# Revit family: HUNTER_PROS-04 Stream, Strip and Bubbler Nozzles
name_source: partatom
category: Sprinklers
revit_build: Autodesk Revit 2017 (Build: 20160225_1515(x64)
units: mm (PartAtom-declared; Revit-internal decimal feet)

## family parameters
Always vertical = Yes
Cut with Voids When Loaded = No
Maintain Annotation Orientation = No
OmniClass Number = 23.11.27.15.11.11
OmniClass Title = Installed Sprinkler Heads
Part Type = Normal
Room Calculation Point = No
Round Connector Dimension = Use Diameter
Shared = Yes
Work Plane-Based = No

## types (18) — shared parameters
Assembly Code = G2050700
Body Height = 155 mm  [stored 0.50853 ft]
Body Material = Hunter® ABS Plastic
Connection_Dia = 15 mm  [stored 0.0492126 ft]
Diameter = 610 mm
Exposed Diameter = 57 mm  [stored 0.187008 ft]
Keynote = 328423.02
Manufacturer = Hunter® Industries
Nozzle URL = https://www.hunterindustries.com
Pop Up Height = 100 mm  [stored 0.328084 ft]
Pop Up Material = Hunter® ABS Plastic
Pressure = 210.0 kPa
Seal = Hunter® White Flex Seal
Show 2D Symbol = Yes
Show Water Spray = Yes
Type Comments = Pro-Spray® PROS-04
Type Image = <None>
URL = https://www.hunterindustries.com
Water = Water

## per-type parameters (varying)
| type | Arc Max | Arc Min | Description | Inlet Size | Model | Nozzle Size | Nozzle_Ref | Trajectory Angle | Trajectory Radius | Water Spray Pattern |
| PROS-04-PCN-25 Blue | 360.00° | 45.00° | ProSpray® PROS-04 10cm PopUp with Pressure Compensating Bubbler (PCN-25) Blue Nozzle | 1/2'' NPT | PROS-04-PCN-25 | Hunter®Pressure Compensating Bubbler Nozzles (PCN-25) Blue Nozzle | 25 | 10.00° | 450 mm  [stored 1.47638 ft] | Water Arc |
| PROS-04-PCN-10 Red | 360.00° | 45.00° | ProSpray® PROS-04 10cm PopUp with Pressure Compensating Bubbler (PCN-10) Red Nozzle | 1/2" NPT | PROS-04-PCN-10 | Hunter®Pressure Compensating Bubbler Nozzles (PCN-10) Red Nozzle | 10 | 10.00° | 450 mm  [stored 1.47638 ft] | Water Arc |
| PROS-04-PCN-20 Yellow | 360.00° | 45.00° | ProSpray® PROS-04 10cm PopUp with Pressure Compensating Bubbler (PCN-20) Yellow Nozzle | 1/2'' NPT | PROS-04-PCN-20 | Hunter®Pressure Compensating Bubbler Nozzles (PCN-20) Yellow Nozzle | 20 | 10.00° | 450 mm  [stored 1.47638 ft] | Water Arc |
| PROS-04-PCN-50 Green | 360.00° | 45.00° | ProSpray® PROS-04 10cm PopUp with Pressure Compensating Bubbler (PCN-50) Green Nozzle | 1/2'' NPT | PROS-04-PCN-50 | Hunter®Pressure Compensating Bubbler Nozzles (PCN-50) Green Nozzle | 50 | 10.00° | 450 mm  [stored 1.47638 ft] | Water Arc |
| PROS-04-MSBN-25Q Blue-0.30m | 90.00° | 90.00° | ProSpray® PROS-04 10cm PopUp with Multi-Stream Bubbler (MSBN-25Q) Blue Nozzle / 90° Arc | 1/2'' NPT | PROS-04-MSBN-25Q | Hunter® Multi-Stream Bubbler Nozzles (MSBN-25Q) Blue Nozzle / 90° Arc | 251 | 25.00° | 300 mm | Water Arc |
| PROS-04-MSBN-50Q Green-0.46m | 90.00° | 90.00° | ProSpray® PROS-04 10cm PopUp with Multi-Stream Bubbler (MSBN-50Q) Green Nozzle / 90° Arc | 1/2'' NPT | PROS-04-MSBN-50Q | Hunter® Multi-Stream Bubbler Nozzles (MSBN-50Q) Green Nozzle / 90° Arc | 501 | 10.00° | 460 mm  [stored 1.50919 ft] | Water Arc |
| PROS-04-MSBN-50H Green-0.30m | 180.00° | 180.00° | ProSpray® PROS-04 10cm PopUp with Multi-Stream Bubbler (MSBN-50H) Green Nozzle / 180° Arc | 1/2'' NPT | PROS-04-MSBN-50H | Hunter® Multi-Stream Bubbler Nozzles (MSBN-50H) Green Nozzle / 180° Arc | 501 | 25.00° | 300 mm | Water Arc |
| PROS-04-MSBN-10H Red-0.46m | 180.00° | 180.00° | ProSpray® PROS-04 10cm PopUp with Multi-Stream Bubbler (MSBN-10H) Red Nozzle / 180° Arc | 1/2'' NPT | PROS-04-MSBN-10H | Hunter® Multi-Stream Bubbler Nozzles (MSBN-10H) Red Nozzle / 180° Arc | 101 | 10.00° | 460 mm  [stored 1.50919 ft] | Water Arc |
| PROS-04-MSBN-10F Red-0.30m | 360.00° | 360.00° | ProSpray® PROS-04 10cm PopUp with Multi-Stream Bubbler (MSBN-10F) Red Nozzle / 360° Arc | 1/2'' NPT | PROS-04-MSBN-10F | Hunter® Multi-Stream Bubbler Nozzles (MSBN-10F) Red Nozzle / 360° Arc | 101 | 25.00° | 300 mm | Water Arc |
| PROS-04-MSBN-20F Yellow-0.46m | 360.00° | 360.00° | ProSpray® PROS-04 10cm PopUp with Multi-Stream Bubbler (MSBN-20F) Yellow Nozzle / 360° Arc | 1/2'' NPT | PROS-04-MSBN-20F | Hunter® Multi-Stream Bubbler Nozzles (MSBN-20F) Yellow Nozzle / 360° Arc | 201 | 10.00° | 460 mm  [stored 1.50919 ft] | Water Arc |
| PROS-04-S-8A-2.4m | 360.00° | 25.00° | ProSpray® PROS-04 10cm PopUp with Stream S-8A Nozzle | 1/2'' NPT | PROS-04-S-8A | Hunter®Stream Nozzle (S-8A) Nozzle | 8 | 5.00° | 2400 mm | Water Arc |
| PROS-04-S-16A-5.0m | 360.00° | 25.00° | ProSpray® PROS-04 10cm PopUp with Stream S-16A Nozzle | 1/2'' NPT | PROS-04-S-16A | Hunter®Stream Nozzle (S-16A) Nozzle | 16 | 5.00° | 5000 mm  [stored 16.4042 ft] | Water Arc |
| PROS-04-LCS515-1.5x4.5m | 1.00° | 1.00° | ProSpray® PROS-04 10cm PopUp with Strip Pattern Left Corner Strip (LCS-515) Nozzle | 1/2'' NPT | PROS-04-LCS515 | Hunter® Strip Pattern Left Corner Strip (LCS-515) Nozzle | 515 | 1.00° | 500 mm  [stored 1.64042 ft] | Water Left Strip 515 |
| PROS-04-RCS515-1.5x4.5m | 1.00° | 1.00° | ProSpray® PROS-04 10cm PopUp with Strip Pattern Right Corner Strip (RCS-515) Nozzle | 1/2'' NPT | PROS-04-RCS515 | Hunter® Strip Pattern Right Corner Strip (RCS-515) Nozzle | 515 | 1.00° | 500 mm  [stored 1.64042 ft] | Water Right Strip515 |
| PROS-04-SS530-1.5x9.1m | 1.00° | 1.00° | ProSpray® PROS-04 10cm PopUp with Strip Pattern Side Strip (SS-530) Nozzle | 1/2'' NPT | PROS-04-SS530 | Hunter® Strip Pattern Side Strip (SS-530) Nozzle | 530 | 1.00° | 500 mm  [stored 1.64042 ft] | Water Side Strip 530 |
| PROS-04-SS918-2.7x5.5m | 1.00° | 1.00° | ProSpray® PROS-04 10cm PopUp with Strip Pattern Side Strip (SS-918) Nozzle | 1/2'' NPT | PROS-04-SS918 | Hunter® Strip Pattern Side Strip (SS-918) Nozzle | 918 | 1.00° | 500 mm  [stored 1.64042 ft] | Water Side Strip 918 |
| PROS-04-CS530-1.5x9.1m | 1.00° | 1.00° | ProSpray® PROS-04 10cm PopUp with Strip Pattern Center Strip (CS-530) Nozzle | 1/2'' NPT | PROS-04-CS530 | Hunter® Strip Pattern Center Strip (CS-530) Nozzle | 530 | 1.00° | 500 mm  [stored 1.64042 ft] | Water Corner Strip 530 |
| PROS-04-ES515-1.5x4.5m | 1.00° | 1.00° | ProSpray® PROS-04 10cm PopUp with Strip Pattern End Strip (ES-515) Nozzle | 1/2'' NPT | PROS-04-ES515 | Hunter® Strip Pattern End Strip (ES-515) Nozzle | 515 | 1.00° | 500 mm  [stored 1.64042 ft] | Water End Strip 515 |

note: [stored X ft] marks values corroborated as IEEE doubles in the binary element streams (Revit-internal decimal feet)

## geometry (parser evidence)
native form markers: Sweep x73
no freeform markers — native parametric forms only
